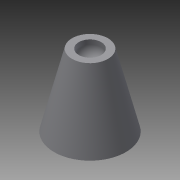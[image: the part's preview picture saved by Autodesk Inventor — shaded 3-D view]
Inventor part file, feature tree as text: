
AUTODESK INVENTOR PART (.ipt)
format: ipt  version: 2013 SP2 (Build 170200200, 200)  size: 103,936 bytes
history: native  units: mm
features: revolve x2, sketch x1
ambient origin geometry x8: Origin, YZ Plane, XZ Plane, XY Plane, X Axis, Y Axis, Z Axis, Center Point
bodies: Solid1 (feature_tree)
feature tree (3):
  revolve  "Revolution1"  [1 undecoded]
  revolve  "Revolution2"  [1 undecoded]
  sketch  "Sketch2"  dims[d0=4.0mm d3=5.0mm d4=1.0mm d5=4.0mm d7=90.0deg d8=3.0mm d9=90.0deg d11=10.0mm d12=16.0mm d13=18.151424mm]
note: 2 required parameter values undecoded (feature->parameter linkage not recoverable at this tier; creation-order binding heuristic only, values carry confidence <= 0.55)
